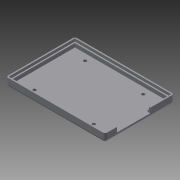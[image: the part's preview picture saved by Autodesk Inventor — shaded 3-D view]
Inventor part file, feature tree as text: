
AUTODESK INVENTOR PART (.ipt)
format: ipt  version: 2015 (Build 190159000, 159)  size: 155,648 bytes
history: native  units: in
note: dims shown in document units (in); Inventor stores cm internally (conversion verified against a paired STEP export)
features: sketch x5, extrude x4, fillet x1, hole x1
ambient origin geometry x8: Origin, YZ Plane, XZ Plane, XY Plane, X Axis, Y Axis, Z Axis, Center Point
bodies: Solid1 (feature_tree)
feature tree (11):
  extrude  "Extrusion1"  Depth=3.622in
  extrude  "Extrusion2"  Depth=0.0984in
  fillet  "Fillet1"  Radius=0.0984in
  extrude  "Extrusion3"  Depth=0.0984in
  hole  "Hole1"  [1 undecoded]
  extrude  "Extrusion4"  Depth=0.0492in
  sketch  "Sketch1"  dims[d0=2.5197in d1=3.622in]
  sketch  "Sketch2"  dims[d2=0.2953in d3=0.0in d4=0.0984in d5=0.0984in]
  sketch  "Sketch3"  dims[d6=0.0984in d7=0.0984in]
  sketch  "Sketch4"  dims[d8=0.2362in d9=0.0in d10=0.0787in]
  sketch  "Sketch5"  dims[d11=0.0492in d12=0.0492in d13=0.0492in d14=0.0492in d15=0.0984in d16=0.0in d17=0.0984in d18=0.0984in d19=0.0984in d20=0.0984in d21=0.5512in d22=0.5118in d23=2.126in d24=3.2283in d25=0.1378in d26=0.1378in d27=0.1181in d28=0.2362in d29=0.1575in d30=0.0787in d31=90.0deg d32=0.315in d33=0.8108in d34=0.0in d35=0.3543in d36=0.7874in d37=0.1772in d38=0.0984in d39=0.0in d41=0.2165in d42=0.0394in d43=0.0591in d44=0.5906in d45=0.689in d46=0.6496in]
note: 1 required parameter value undecoded (feature->parameter linkage not recoverable at this tier; creation-order binding heuristic only, values carry confidence <= 0.55)
